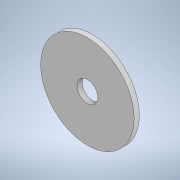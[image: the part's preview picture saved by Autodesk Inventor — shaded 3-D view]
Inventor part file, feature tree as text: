
AUTODESK INVENTOR PART (.ipt)
format: ipt  version: 2021 (Build 250183000, 183)  size: 95,744 bytes
history: native  units: mm
features: extrude x1, sketch x1
ambient origin geometry x8: Origin, YZ Plane, XZ Plane, XY Plane, X Axis, Y Axis, Z Axis, Center Point
bodies: Solid1 (feature_tree)
feature tree (2):
  extrude  "Extrusion1"  Depth=1.0mm
  sketch  "Sketch1"  dims[d0=4.0mm d1=18.0mm d2=1.0mm d3=0.0mm]
